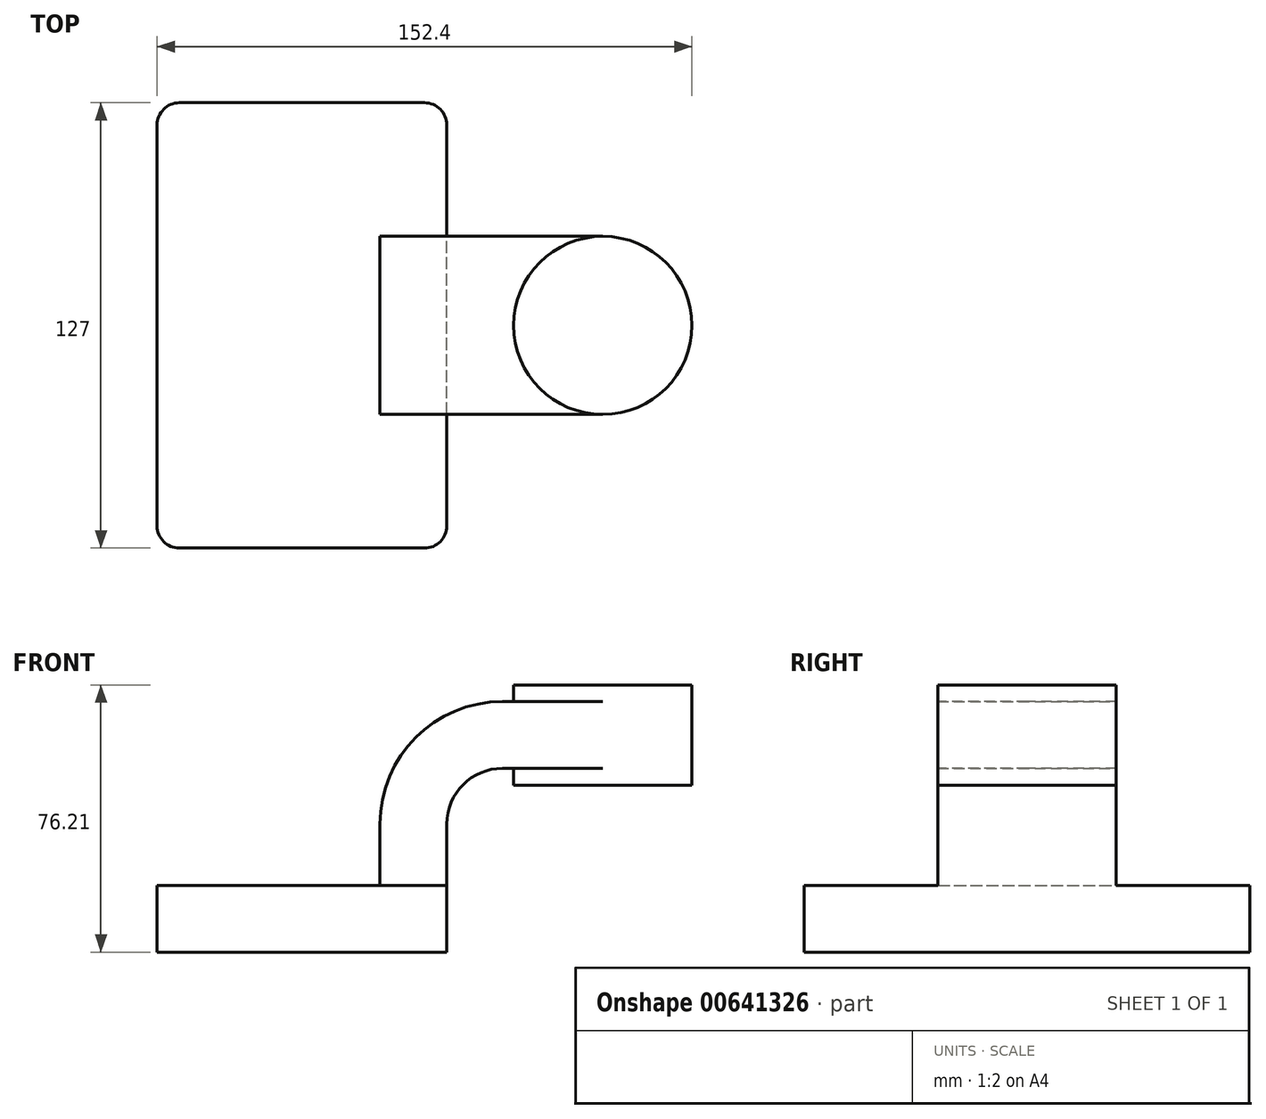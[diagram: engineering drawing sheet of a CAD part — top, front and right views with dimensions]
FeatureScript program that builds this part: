
annotation { "Feature Type Name" : "Feature", "Feature Type Description" : "" }
export const myFeature = defineFeature(function(context is Context, id is Id, definition is map)
    precondition{}
    {
        {
            var Q0;
            Q0=qCreatedBy(makeId("Front.planeOp"),FACE);
            var sketch = newSketch(context, id + "F0", { "sketchPlane" : qUnion([Q0])});
            skLineSegment(sketch, "E0.bottom", {"start": v(41.27, 9.53) * mm, "end": v(-41.28, 9.52) * mm});
            skLineSegment(sketch, "E0.top", {"start": v(41.28, -9.53) * mm, "end": v(-41.28, -9.53) * mm});
            skLineSegment(sketch, "E0.left", {"start": v(41.28, 9.53) * mm, "end": v(41.28, -9.53) * mm});
            skLineSegment(sketch, "E0.right", {"start": v(-41.28, 9.52) * mm, "end": v(-41.28, -9.53) * mm});
            skPoint(sketch, "E0.middle", {"position": v(0, 0) * mm});
            skLineSegment(sketch, "E1.bottom", {"start": v(60.32, 38.1) * mm, "end": v(111.12, 38.1) * mm});
            skLineSegment(sketch, "E1.top", {"start": v(60.32, 66.67) * mm, "end": v(111.12, 66.67) * mm});
            skLineSegment(sketch, "E1.left", {"start": v(60.32, 38.1) * mm, "end": v(60.32, 66.68) * mm});
            skLineSegment(sketch, "E1.right", {"start": v(111.12, 38.1) * mm, "end": v(111.12, 66.68) * mm});
            skPoint(sketch, "E1.middle", {"position": v(85.72, 52.39) * mm});
            skLineSegment(sketch, "E2", {"start": v(41.27, 9.53) * mm, "end": v(41.27, 27) * mm});
            skArc(sketch, "E3", {"start": v(41.27, 27) * mm, "mid": v(45.92, 38.23) * mm, "end": v(57.15, 42.88) * mm});
            skLineSegment(sketch, "E4", {"start": v(57.15, 42.88) * mm, "end": v(93.98, 42.88) * mm});
            skLineSegment(sketch, "E5.0", {"start": v(57.15, 61.93) * mm, "end": v(93.98, 61.93) * mm});
            skArc(sketch, "E5.1", {"start": v(22.22, 27) * mm, "mid": v(32.45, 51.7) * mm, "end": v(57.15, 61.93) * mm});
            skLineSegment(sketch, "E5.2", {"start": v(22.22, 9.53) * mm, "end": v(22.22, 27) * mm});
            skLineSegment(sketch, "E6", {"start": v(93.98, 42.88) * mm, "end": v(93.98, 66.67) * mm});
            skFitSpline(sketch, "E7", {"points": [v(-41.28, 9.52) * mm, v(57.15, 61.93) * mm], "startDerivative": vector(68.27, 151.02) * mm, "endDerivative": vector(171.45, 0) * mm});
            skLineSegment(sketch, "E8", {"start": v(85.72, 38.1) * mm, "end": v(85.72, 66.67) * mm});
            skSolve(sketch);
        }
        {
            var Q0;
            Q0=makeQuery(id+"F0.imprint","IMPRINT",FACE,{"disambiguationData":[TD([[makeQuery(id+"F0.imprint","IMPRINT",EDGE,{"derivedFrom":sQuery(id+"F0.wireOp",EDGE,"E0.top")}),-1.0]])]});
            extrude(context, id + "F1", {"entities" : qUnion([Q0]), "endBound" : BoundingType.SYMMETRIC, "depth" : 127 * mm, "offsetDistance" : 25.4 * mm});
        }
        {
            var Q0;
            {var subQ1=sQuery(id+"F0.wireOp",EDGE,"E2");Q0=makeQuery(id+"F0.imprint","IMPRINT",FACE,{"disambiguationData":[TD([[makeQuery(id+"F0.imprint","IMPRINT",EDGE,{"derivedFrom":subQ1}),1.0]])]});}
            var Q1;
            {var subQ0=sQuery(id+"F0.wireOp",EDGE,"E4");var subQ1=sQuery(id+"F0.wireOp",EDGE,"E1.left");var subQ2=makeQuery(id+"F0.imprint","INTERSECT",VERTEX,{"derivedFrom":[subQ1,subQ0]});Q1=makeQuery(id+"F0.imprint","IMPRINT",FACE,{"disambiguationData":[TD([[makeQuery(id+"F0.imprint","IMPRINT",EDGE,{"disambiguationData":[TD([[subQ2,-1.0]])],"derivedFrom":subQ1}),-1.0]])]});}
            extrude(context, id + "F2", {"entities" : qUnion([Q0, Q1]), "operationType" : NewBodyOperationType.ADD, "endBound" : BoundingType.SYMMETRIC, "depth" : 50.8 * mm, "offsetDistance" : 25.4 * mm});
        }
        {
            var Q0;
            {var subQ0=sQuery(id+"F0.wireOp",EDGE,"E6");var subQ1=sQuery(id+"F0.wireOp",EDGE,"E1.top");var subQ2=makeQuery(id+"F0.imprint","INTERSECT",VERTEX,{"derivedFrom":[subQ1,subQ0]});Q0=makeQuery(id+"F0.imprint","IMPRINT",FACE,{"disambiguationData":[TD([[makeQuery(id+"F0.imprint","IMPRINT",EDGE,{"disambiguationData":[TD([[subQ2,1.0]])],"derivedFrom":subQ1}),-1.0]])]});}
            var Q1;
            {var subQ0=sQuery(id+"F0.wireOp",EDGE,"E6");var subQ1=sQuery(id+"F0.wireOp",EDGE,"E4");var subQ2=makeQuery(id+"F0.imprint","INTERSECT",VERTEX,{"derivedFrom":[subQ1,subQ0]});Q1=makeQuery(id+"F0.imprint","IMPRINT",FACE,{"disambiguationData":[TD([[makeQuery(id+"F0.imprint","IMPRINT",EDGE,{"disambiguationData":[TD([[subQ2,1.0]])],"derivedFrom":subQ1}),1.0]])]});}
            var Q2;
            {var subQ5=sQuery(id+"F0.wireOp",EDGE,"E1.right");Q2=makeQuery(id+"F0.imprint","IMPRINT",FACE,{"disambiguationData":[TD([[makeQuery(id+"F0.imprint","IMPRINT",EDGE,{"derivedFrom":subQ5}),1.0]])]});}
            var Q3;
            Q3=sQuery(id+"F0.wireOp",EDGE,"E8");
            revolve(context, id + "F3", {"operationType" : NewBodyOperationType.ADD, "entities" : qUnion([Q0, Q1, Q2]), "axis" : qUnion([Q3]), "revolveType" : RevolveType.FULL});
        }
        {
            var Q0;
            Q0=makeQuery(id+"F0.imprint","IMPRINT",FACE,{"disambiguationData":[TD([[makeQuery(id+"F0.imprint","IMPRINT",EDGE,{"derivedFrom":sQuery(id+"F0.wireOp",EDGE,"E5.1")}),1.0]])]});
            extrude(context, id + "F4", {"entities" : qUnion([Q0]), "operationType" : NewBodyOperationType.ADD, "endBound" : BoundingType.SYMMETRIC, "depth" : 15.88 * mm, "offsetDistance" : 25.4 * mm});
        }
        {
            var Q0;
            Q0=makeQuery(id+"F1.opExtrude","CAP_EDGE",EDGE,{"disambiguationData":[OSD([sQuery(id+"F0.wireOp",EDGE,"E0.left")])],"isStart":false});
            var Q1;
            Q1=makeQuery(id+"F1.opExtrude","CAP_EDGE",EDGE,{"disambiguationData":[OSD([sQuery(id+"F0.wireOp",EDGE,"E0.right")])],"isStart":false});
            var Q2;
            Q2=makeQuery(id+"F1.opExtrude","CAP_EDGE",EDGE,{"disambiguationData":[OSD([sQuery(id+"F0.wireOp",EDGE,"E0.left")])],"isStart":true});
            var Q3;
            Q3=makeQuery(id+"F1.opExtrude","CAP_EDGE",EDGE,{"disambiguationData":[OSD([sQuery(id+"F0.wireOp",EDGE,"E0.right")])],"isStart":true});
            fillet(context, id + "F5", {"entities" : qUnion([Q0, Q1, Q2, Q3]), "radius" : 6.35 * mm, "tangentPropagation" : true, "allowEdgeOverflow" : false});
        }
    });
